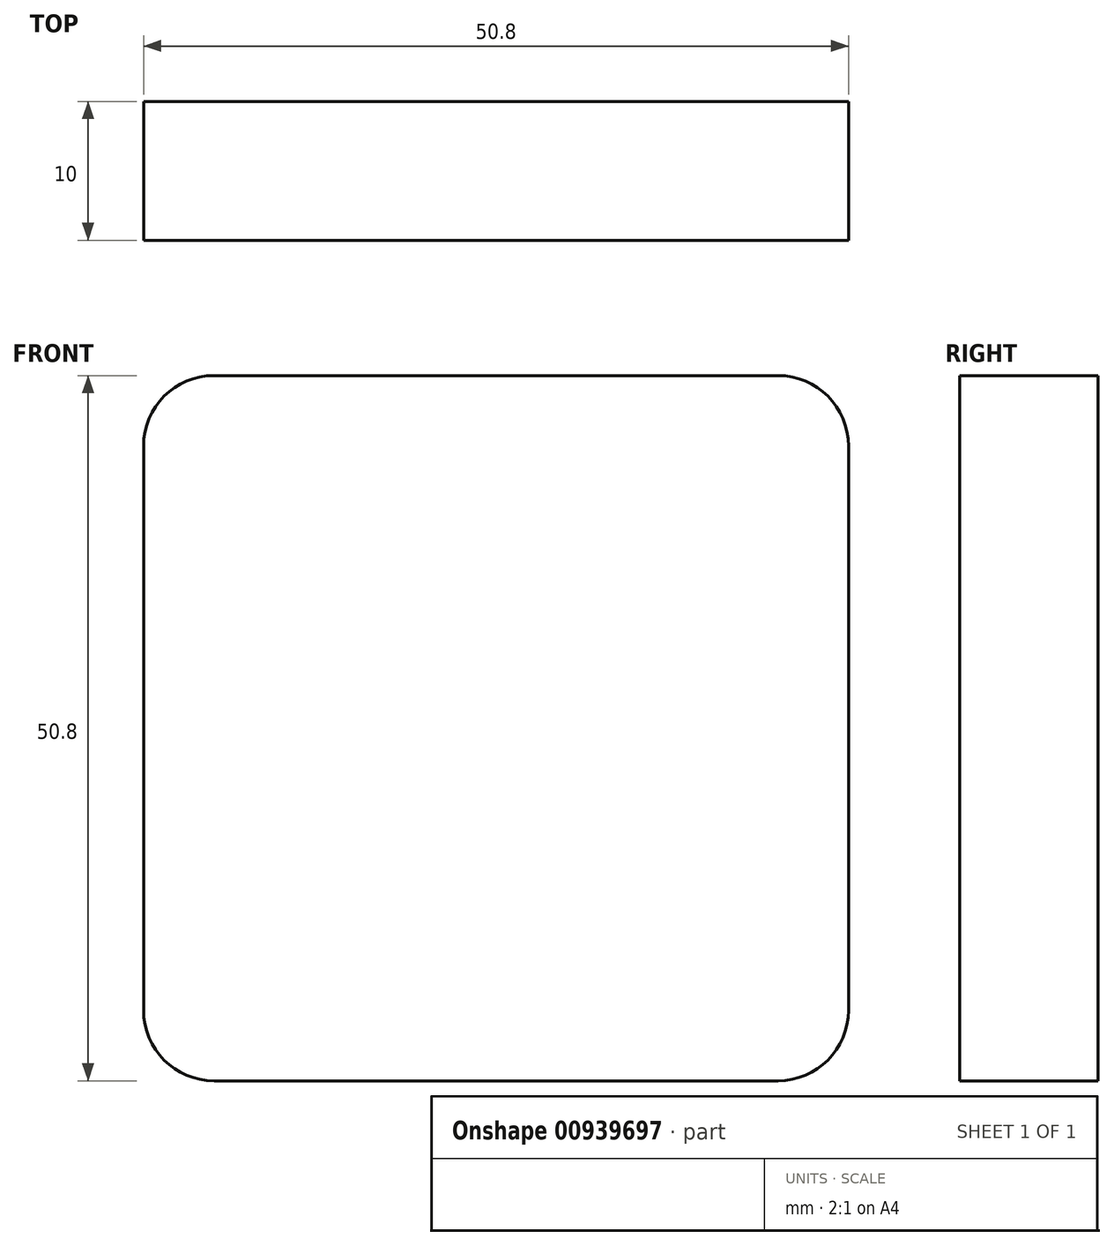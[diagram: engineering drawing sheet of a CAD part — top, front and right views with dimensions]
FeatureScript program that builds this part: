
annotation { "Feature Type Name" : "Feature", "Feature Type Description" : "" }
export const myFeature = defineFeature(function(context is Context, id is Id, definition is map)
    precondition{}
    {
        {
            var Q0;
            Q0=qCreatedBy(makeId("Front.planeOp"),FACE);
            var sketch = newSketch(context, id + "F0", { "sketchPlane" : qUnion([Q0])});
            skLineSegment(sketch, "E0.bottom", {"start": v(25.4, -25.4) * mm, "end": v(-25.4, -25.4) * mm});
            skLineSegment(sketch, "E0.top", {"start": v(25.4, 25.4) * mm, "end": v(-25.4, 25.4) * mm});
            skLineSegment(sketch, "E0.left", {"start": v(25.4, -25.4) * mm, "end": v(25.4, 25.4) * mm});
            skLineSegment(sketch, "E0.right", {"start": v(-25.4, -25.4) * mm, "end": v(-25.4, 25.4) * mm});
            skPoint(sketch, "E0.middle", {"position": v(0, 0) * mm});
            skSolve(sketch);
        }
        {
            var Q0;
            Q0 = qSketchRegion(id + "F0", true);
            extrude(context, id + "F1", {"entities" : qUnion([Q0]), "depth" : 5 * mm, "offsetDistance" : 25.4 * mm, "hasSecondDirection" : true, "secondDirectionOppositeDirection" : true, "secondDirectionDepth" : 5 * mm});
        }
        {
            var Q0;
            Q0=makeQuery(id+"F1.opExtrude","SWEPT_EDGE",EDGE,{"disambiguationData":[OSD([sQuery(id+"F0.wireOp",EDGE,"E0.top"),sQuery(id+"F0.wireOp",EDGE,"E0.left")])]});
            var Q1;
            Q1=makeQuery(id+"F1.opExtrude","SWEPT_EDGE",EDGE,{"disambiguationData":[OSD([sQuery(id+"F0.wireOp",EDGE,"E0.top"),sQuery(id+"F0.wireOp",EDGE,"E0.right")])]});
            var Q2;
            Q2=makeQuery(id+"F1.opExtrude","SWEPT_EDGE",EDGE,{"disambiguationData":[OSD([sQuery(id+"F0.wireOp",EDGE,"E0.bottom"),sQuery(id+"F0.wireOp",EDGE,"E0.left")])]});
            var Q3;
            Q3=makeQuery(id+"F1.opExtrude","SWEPT_EDGE",EDGE,{"disambiguationData":[OSD([sQuery(id+"F0.wireOp",EDGE,"E0.bottom"),sQuery(id+"F0.wireOp",EDGE,"E0.right")])]});
            fillet(context, id + "F2", {"entities" : qUnion([Q0, Q1, Q2, Q3]), "radius" : 5.08 * mm, "tangentPropagation" : true, "allowEdgeOverflow" : false});
        }
    });
